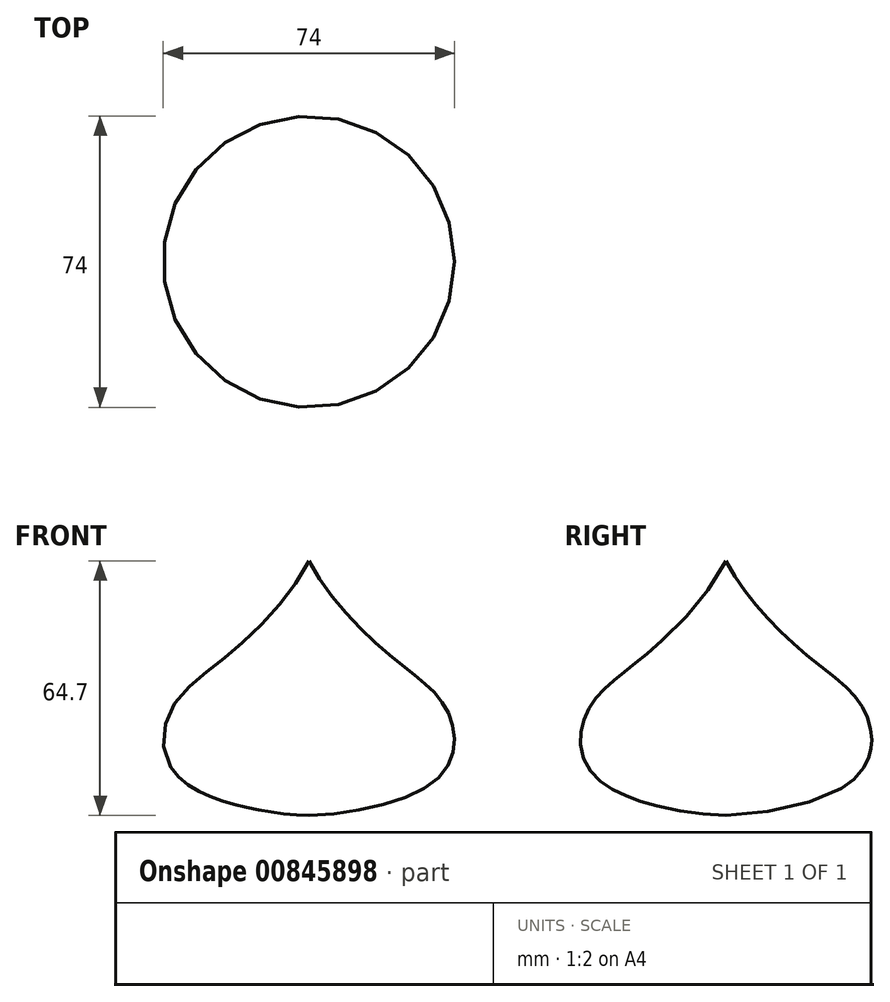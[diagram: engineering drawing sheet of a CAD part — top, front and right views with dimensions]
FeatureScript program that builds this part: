
annotation { "Feature Type Name" : "Feature", "Feature Type Description" : "" }
export const myFeature = defineFeature(function(context is Context, id is Id, definition is map)
    precondition{}
    {
        {
            var Q0;
            Q0=qCreatedBy(makeId("Front.planeOp"),FACE);
            var sketch = newSketch(context, id + "F0", { "sketchPlane" : qUnion([Q0])});
            skLineSegment(sketch, "E0", {"start": v(0, 75.67) * mm, "end": v(0, -74.93) * mm});
            skFitSpline(sketch, "E1", {"points": [v(25.4, 43.52) * mm, v(15.8, 40.37) * mm, v(-3.23, 14.7) * mm, v(19.68, -20.97) * mm, v(35.02, -35.57) * mm, v(32.43, -53.3) * mm, v(-17.83, -60.52) * mm, v(-23.74, -53.68) * mm, v(-14.14, -50.9) * mm, v(0, -54.6) * mm, v(11.55, -52.75) * mm, v(27.44, -46.29) * mm, v(22.64, -35.2) * mm, v(0, -15.61) * mm, v(-14.32, 9.89) * mm, v(-7.3, 38.16) * mm, v(14.5, 51.65) * mm, v(25.4, 43.52) * mm]});
            skSolve(sketch);
        }
        {
            var Q0;
            {var subQ0=sQuery(id+"F0.wireOp",EDGE,"E1");var subQ1=sQuery(id+"F0.wireOp",EDGE,"E0");var subQ2=makeQuery(id+"F0.imprint","INTERSECT",VERTEX,{"disambiguationData":[OD(0.0)],"derivedFrom":[subQ1,subQ0]});Q0=makeQuery(id+"F0.imprint","IMPRINT",FACE,{"disambiguationData":[TD([[makeQuery(id+"F0.imprint","IMPRINT",EDGE,{"disambiguationData":[TD([[subQ2,-1.0]])],"derivedFrom":subQ1}),1.0]])]});}
            var Q1;
            {var subQ0=sQuery(id+"F0.wireOp",EDGE,"E1");var subQ1=sQuery(id+"F0.wireOp",EDGE,"E0");var subQ2=makeQuery(id+"F0.imprint","INTERSECT",VERTEX,{"disambiguationData":[OD(3.0)],"derivedFrom":[subQ1,subQ0]});Q1=makeQuery(id+"F0.imprint","IMPRINT",FACE,{"disambiguationData":[TD([[makeQuery(id+"F0.imprint","IMPRINT",EDGE,{"disambiguationData":[TD([[subQ2,-1.0]])],"derivedFrom":subQ1}),1.0]])]});}
            var Q2;
            Q2=sQuery(id+"F0.wireOp",EDGE,"E0");
            revolve(context, id + "F1", {"surfaceOperationType" : NewSurfaceOperationType.NEW, "entities" : qUnion([Q0, Q1]), "axis" : qUnion([Q2]), "revolveType" : RevolveType.FULL});
        }
    });
